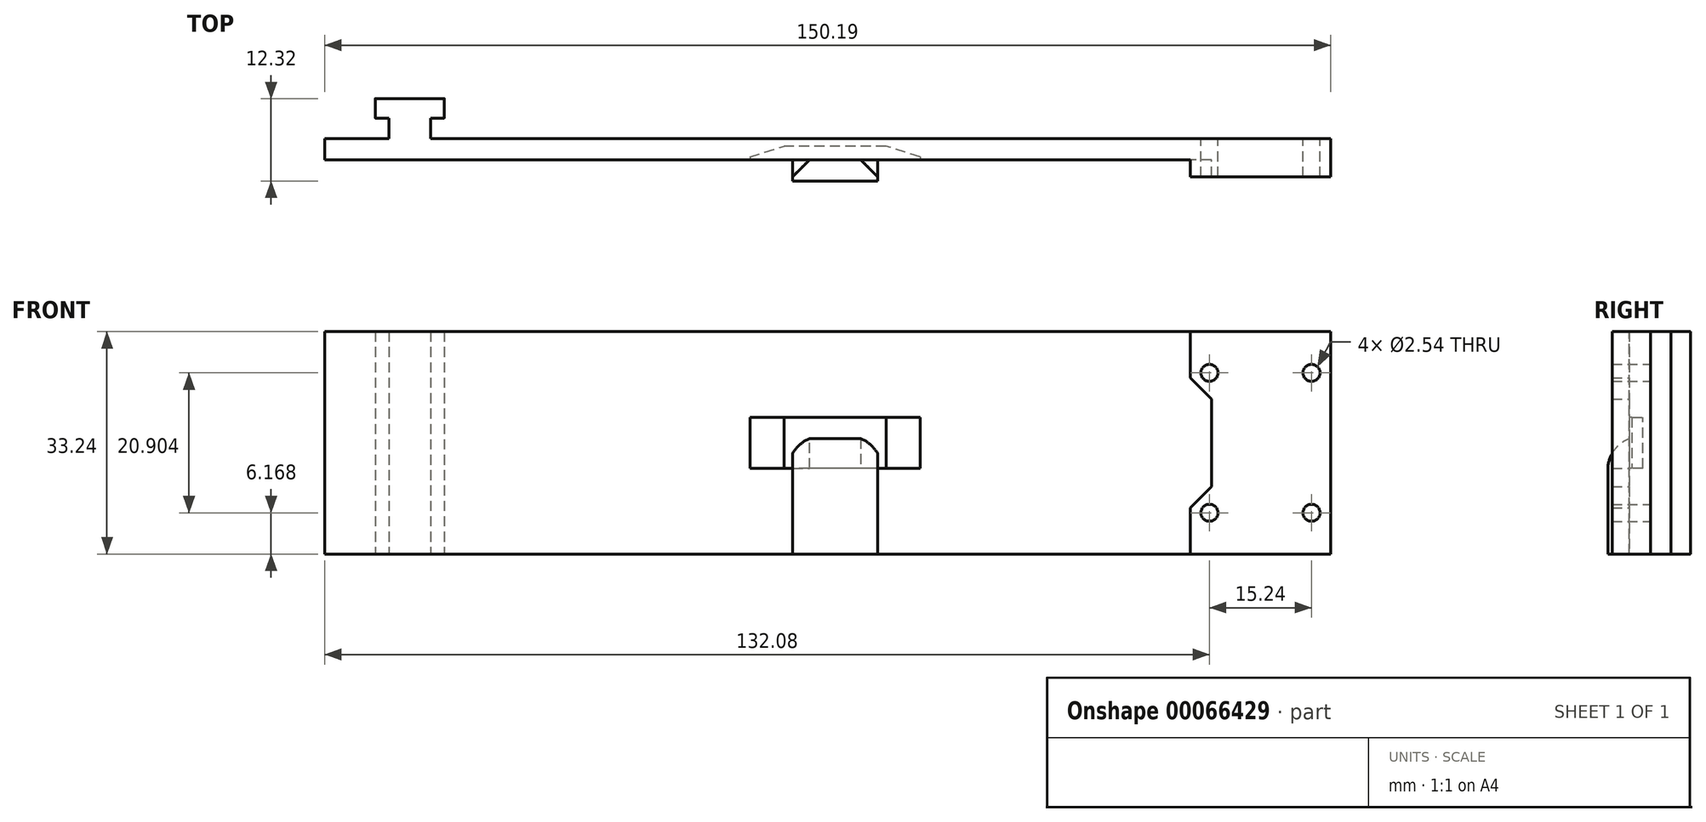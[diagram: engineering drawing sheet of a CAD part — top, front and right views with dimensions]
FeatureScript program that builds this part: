
annotation { "Feature Type Name" : "Feature", "Feature Type Description" : "" }
export const myFeature = defineFeature(function(context is Context, id is Id, definition is map)
    precondition{}
    {
        {
            var Q0;
            Q0=qCreatedBy(makeId("Front.planeOp"),FACE);
            var sketch = newSketch(context, id + "F0", { "sketchPlane" : qUnion([Q0])});
            skLineSegment(sketch, "E0.rect.bottom", {"start": v(5.16, 16.62) * mm, "end": v(-5.16, 16.62) * mm});
            skLineSegment(sketch, "E0.rect.top", {"start": v(5.16, -16.62) * mm, "end": v(-5.16, -16.62) * mm});
            skLineSegment(sketch, "E0.rect.left", {"start": v(5.16, 16.62) * mm, "end": v(5.16, -16.62) * mm});
            skLineSegment(sketch, "E0.rect.right", {"start": v(-5.16, 16.62) * mm, "end": v(-5.16, -16.62) * mm});
            skPoint(sketch, "E0.rect.middle", {"position": v(0, 0) * mm});
            skSolve(sketch);
        }
        {
            var Q0;
            Q0 = qSketchRegion(id + "F0", true);
            extrude(context, id + "F1", {"entities" : qUnion([Q0]), "depth" : 2.92 * mm, "offsetDistance" : 25.4 * mm});
        }
        {
            var Q0;
            Q0=makeQuery(id+"F1.opExtrude","CAP_FACE",FACE,{"disambiguationData":[OSD([sQuery(id+"F0.wireOp",EDGE,"E0.rect.bottom"),sQuery(id+"F0.wireOp",EDGE,"E0.rect.top"),sQuery(id+"F0.wireOp",EDGE,"E0.rect.left"),sQuery(id+"F0.wireOp",EDGE,"E0.rect.right")])],"isStart":false});
            var sketch = newSketch(context, id + "F2", { "sketchPlane" : qUnion([Q0])});
            skLineSegment(sketch, "E1.rect.bottom", {"start": v(3.1, 16.62) * mm, "end": v(-3.1, 16.62) * mm});
            skLineSegment(sketch, "E1.rect.top", {"start": v(3.1, -16.62) * mm, "end": v(-3.1, -16.62) * mm});
            skLineSegment(sketch, "E1.rect.left", {"start": v(3.1, 16.62) * mm, "end": v(3.1, -16.62) * mm});
            skLineSegment(sketch, "E1.rect.right", {"start": v(-3.1, 16.62) * mm, "end": v(-3.1, -16.62) * mm});
            skPoint(sketch, "E1.rect.middle", {"position": v(0, 0) * mm});
            skSolve(sketch);
        }
        {
            var Q0;
            Q0 = qSketchRegion(id + "F2", true);
            extrude(context, id + "F3", {"entities" : qUnion([Q0]), "operationType" : NewBodyOperationType.ADD, "depth" : 3.05 * mm, "offsetDistance" : 25.4 * mm});
        }
        {
            var Q0;
            Q0=makeQuery(id+"F3.opExtrude","CAP_FACE",FACE,{"disambiguationData":[OSD([sQuery(id+"F2.wireOp",EDGE,"E1.rect.bottom"),sQuery(id+"F2.wireOp",EDGE,"E1.rect.top"),sQuery(id+"F2.wireOp",EDGE,"E1.rect.left"),sQuery(id+"F2.wireOp",EDGE,"E1.rect.right")])],"isStart":false});
            var sketch = newSketch(context, id + "F4", { "sketchPlane" : qUnion([Q0])});
            skLineSegment(sketch, "E2.bottom", {"start": v(-12.7, -16.62) * mm, "end": v(137.5, -16.62) * mm});
            skLineSegment(sketch, "E2.top", {"start": v(-12.7, 16.62) * mm, "end": v(137.5, 16.62) * mm});
            skLineSegment(sketch, "E2.left", {"start": v(-12.7, -16.62) * mm, "end": v(-12.7, 16.62) * mm});
            skLineSegment(sketch, "E2.right", {"start": v(137.5, -16.62) * mm, "end": v(137.5, 16.62) * mm});
            skCircle(sketch, "E3", {"center": v(134.62, 10.45) * mm, "radius": 1.27 * mm});
            skCircle(sketch, "E4", {"center": v(134.62, -10.45) * mm, "radius": 1.27 * mm});
            skCircle(sketch, "E5", {"center": v(119.38, -10.45) * mm, "radius": 1.27 * mm});
            skCircle(sketch, "E6", {"center": v(119.38, 10.45) * mm, "radius": 1.27 * mm});
            skLineSegment(sketch, "E7", {"start": v(119.38, -10.45) * mm, "end": v(134.62, -10.45) * mm, "construction": true});
            skPoint(sketch, "E8", {"position": v(127, -10.45) * mm});
            skLineSegment(sketch, "E9", {"start": v(134.62, 10.45) * mm, "end": v(134.62, -10.45) * mm, "construction": true});
            skPoint(sketch, "E10", {"position": v(134.62, 0) * mm});
            skSolve(sketch);
        }
        {
            var Q0;
            Q0 = qSketchRegion(id + "F4", true);
            extrude(context, id + "F5", {"entities" : qUnion([Q0]), "operationType" : NewBodyOperationType.ADD, "depth" : 3.17 * mm});
        }
        {
            var Q0;
            Q0=makeQuery(id+"F1.opExtrude","CAP_EDGE",EDGE,{"disambiguationData":[OSD([sQuery(id+"F0.wireOp",EDGE,"E0.rect.left")])],"isStart":false});
            var Q1;
            Q1=makeQuery(id+"F1.opExtrude","CAP_EDGE",EDGE,{"disambiguationData":[OSD([sQuery(id+"F0.wireOp",EDGE,"E0.rect.left")])],"isStart":true});
            var Q2;
            Q2=makeQuery(id+"F1.opExtrude","CAP_EDGE",EDGE,{"disambiguationData":[OSD([sQuery(id+"F0.wireOp",EDGE,"E0.rect.right")])],"isStart":false});
            var Q3;
            Q3=makeQuery(id+"F1.opExtrude","CAP_EDGE",EDGE,{"disambiguationData":[OSD([sQuery(id+"F0.wireOp",EDGE,"E0.rect.right")])],"isStart":true});
            var Q4;
            Q4=makeQuery(id+"F1.opExtrude","CAP_EDGE",EDGE,{"disambiguationData":[OSD([sQuery(id+"F0.wireOp",EDGE,"E0.rect.top")])],"isStart":true});
            var Q5;
            Q5=makeQuery(id+"F1.opExtrude","CAP_EDGE",EDGE,{"disambiguationData":[OSD([sQuery(id+"F0.wireOp",EDGE,"E0.rect.bottom")])],"isStart":true});
            fillet(context, id + "F6", {"entities" : qUnion([Q0, Q1, Q2, Q3, Q4, Q5]), "radius" : .63 / 50.8 * mm, "tangentPropagation" : true, "allowEdgeOverflow" : false});
        }
        {
            var Q0;
            Q0=makeQuery(id+"F5.opExtrude","CAP_FACE",FACE,{"disambiguationData":[OSD([sQuery(id+"F4.wireOp",EDGE,"E2.bottom"),sQuery(id+"F4.wireOp",EDGE,"E2.top"),sQuery(id+"F4.wireOp",EDGE,"E2.left"),sQuery(id+"F4.wireOp",EDGE,"E2.right"),sQuery(id+"F4.wireOp",EDGE,"E3"),sQuery(id+"F4.wireOp",EDGE,"E4"),sQuery(id+"F4.wireOp",EDGE,"E5"),sQuery(id+"F4.wireOp",EDGE,"E6")])],"isStart":false});
            var sketch = newSketch(context, id + "F7", { "sketchPlane" : qUnion([Q0])});
            skLineSegment(sketch, "E11.rect.bottom", {"start": v(76.2, 3.81) * mm, "end": v(50.8, 3.81) * mm});
            skLineSegment(sketch, "E11.rect.top", {"start": v(76.2, -3.8) * mm, "end": v(50.8, -3.8) * mm});
            skLineSegment(sketch, "E11.rect.left", {"start": v(76.2, 3.81) * mm, "end": v(76.2, -3.8) * mm});
            skLineSegment(sketch, "E11.rect.right", {"start": v(50.8, 3.81) * mm, "end": v(50.8, -3.8) * mm});
            skPoint(sketch, "E11.rect.middle", {"position": v(63.5, 0) * mm});
            skLineSegment(sketch, "E12", {"start": v(0, 0) * mm, "end": v(63.5, 0) * mm, "construction": true});
            skSolve(sketch);
        }
        {
            var Q0;
            Q0 = qSketchRegion(id + "F7", true);
            extrude(context, id + "F8", {"entities" : qUnion([Q0]), "operationType" : NewBodyOperationType.REMOVE, "oppositeDirection" : true, "depth" : 2.03 * mm});
        }
        {
            var Q0;
            Q0=makeQuery(id+"F8.boolean.opBoolean","COPY",EDGE,{"derivedFrom":makeQuery(id+"F8.opExtrude","CAP_EDGE",EDGE,{"disambiguationData":[OSD([sQuery(id+"F7.wireOp",EDGE,"E11.rect.right")])],"isStart":false})});
            var Q1;
            Q1=makeQuery(id+"F8.boolean.opBoolean","COPY",EDGE,{"derivedFrom":makeQuery(id+"F8.opExtrude","CAP_EDGE",EDGE,{"disambiguationData":[OSD([sQuery(id+"F7.wireOp",EDGE,"E11.rect.left")])],"isStart":false})});
            chamfer(context, id + "F9", {"entities" : qUnion([Q0, Q1]), "chamferType" : ChamferType.TWO_OFFSETS, "width1" : 5.08 * mm, "oppositeDirection" : false, "width2" : 1.6 * mm, "tangentPropagation" : true});
        }
        {
            var Q0;
            Q0=makeQuery(id+"F5.opExtrude","CAP_FACE",FACE,{"disambiguationData":[OSD([sQuery(id+"F4.wireOp",EDGE,"E2.bottom"),sQuery(id+"F4.wireOp",EDGE,"E2.top"),sQuery(id+"F4.wireOp",EDGE,"E2.left"),sQuery(id+"F4.wireOp",EDGE,"E2.right"),sQuery(id+"F4.wireOp",EDGE,"E3"),sQuery(id+"F4.wireOp",EDGE,"E4"),sQuery(id+"F4.wireOp",EDGE,"E5"),sQuery(id+"F4.wireOp",EDGE,"E6")])],"isStart":false});
            var sketch = newSketch(context, id + "F10", { "sketchPlane" : qUnion([Q0])});
            skLineSegment(sketch, "E13.bottom", {"start": v(57.15, -16.62) * mm, "end": v(69.85, -16.62) * mm});
            skLineSegment(sketch, "E13.top", {"start": v(57.15, 0.64) * mm, "end": v(69.85, 0.64) * mm});
            skLineSegment(sketch, "E13.left", {"start": v(57.15, -16.62) * mm, "end": v(57.15, 0.64) * mm});
            skLineSegment(sketch, "E13.right", {"start": v(69.85, -16.62) * mm, "end": v(69.85, 0.64) * mm});
            skPoint(sketch, "E14", {"position": v(63.5, -3.8) * mm});
            skPoint(sketch, "E15", {"position": v(63.5, 0.64) * mm});
            skSolve(sketch);
        }
        {
            var Q0;
            Q0 = qSketchRegion(id + "F10", true);
            extrude(context, id + "F11", {"entities" : qUnion([Q0]), "operationType" : NewBodyOperationType.ADD, "depth" : 3.17 * mm});
        }
        {
            var Q0;
            Q0=makeQuery(id+"F11.opExtrude","CAP_EDGE",EDGE,{"disambiguationData":[OSD([sQuery(id+"F10.wireOp",EDGE,"E13.top")])],"isStart":false});
            fillet(context, id + "F12", {"entities" : qUnion([Q0]), "radius" : 5.08 * mm, "tangentPropagation" : true, "allowEdgeOverflow" : false});
        }
        {
            var Q0;
            Q0=makeQuery(id+"F5.opExtrude","CAP_FACE",FACE,{"disambiguationData":[OSD([sQuery(id+"F4.wireOp",EDGE,"E2.bottom"),sQuery(id+"F4.wireOp",EDGE,"E2.top"),sQuery(id+"F4.wireOp",EDGE,"E2.left"),sQuery(id+"F4.wireOp",EDGE,"E2.right"),sQuery(id+"F4.wireOp",EDGE,"E3"),sQuery(id+"F4.wireOp",EDGE,"E4"),sQuery(id+"F4.wireOp",EDGE,"E5"),sQuery(id+"F4.wireOp",EDGE,"E6")])],"isStart":false});
            var sketch = newSketch(context, id + "F13", { "sketchPlane" : qUnion([Q0])});
            skCircle(sketch, "E16", {"center": v(119.38, 10.45) * mm, "radius": 1.27 * mm});
            skCircle(sketch, "E17", {"center": v(134.62, 10.45) * mm, "radius": 1.27 * mm});
            skCircle(sketch, "E18", {"center": v(119.38, -10.45) * mm, "radius": 1.27 * mm});
            skCircle(sketch, "E19", {"center": v(134.62, -10.45) * mm, "radius": 1.27 * mm});
            skLineSegment(sketch, "E20.bottom", {"start": v(137.5, 16.62) * mm, "end": v(116.5, 16.62) * mm});
            skLineSegment(sketch, "E20.top", {"start": v(137.5, -16.62) * mm, "end": v(116.5, -16.62) * mm});
            skLineSegment(sketch, "E20.left", {"start": v(137.5, 16.62) * mm, "end": v(137.5, -16.62) * mm});
            skLineSegment(sketch, "E21", {"start": v(116.5, 16.62) * mm, "end": v(116.5, 9.73) * mm});
            skLineSegment(sketch, "E22", {"start": v(116.5, 9.73) * mm, "end": v(119.68, 6.56) * mm});
            skLineSegment(sketch, "E23", {"start": v(119.68, 6.56) * mm, "end": v(119.68, -6.56) * mm});
            skLineSegment(sketch, "E24", {"start": v(119.68, -6.56) * mm, "end": v(116.5, -9.73) * mm});
            skLineSegment(sketch, "E25", {"start": v(116.5, -9.73) * mm, "end": v(116.5, -16.62) * mm});
            skSolve(sketch);
        }
        {
            var Q0;
            Q0 = qSketchRegion(id + "F13", true);
            extrude(context, id + "F14", {"entities" : qUnion([Q0]), "operationType" : NewBodyOperationType.ADD, "depth" : 2.54 * mm});
        }
        {
            var Q0;
            {var subQ0=sQuery(id+"F10.wireOp",EDGE,"E13.right");Q0=makeQuery(id+"F11.boolean.opBoolean","SPLIT",EDGE,{"disambiguationData":[topologyDisambiguationEdgeConnected([makeQuery(id+"F5.opExtrude","CAP_FACE",FACE,{"disambiguationData":[OSD([sQuery(id+"F4.wireOp",EDGE,"E2.bottom"),sQuery(id+"F4.wireOp",EDGE,"E2.top"),sQuery(id+"F4.wireOp",EDGE,"E2.left"),sQuery(id+"F4.wireOp",EDGE,"E2.right"),sQuery(id+"F4.wireOp",EDGE,"E3"),sQuery(id+"F4.wireOp",EDGE,"E4"),sQuery(id+"F4.wireOp",EDGE,"E5"),sQuery(id+"F4.wireOp",EDGE,"E6")])],"isStart":false})])],"derivedFrom":makeQuery(id+"F11.opExtrude","CAP_EDGE",EDGE,{"disambiguationData":[OSD([subQ0])],"isStart":true})});}
            var Q1;
            {var subQ0=sQuery(id+"F10.wireOp",EDGE,"E13.left");Q1=makeQuery(id+"F11.boolean.opBoolean","SPLIT",EDGE,{"disambiguationData":[topologyDisambiguationEdgeConnected([makeQuery(id+"F5.opExtrude","CAP_FACE",FACE,{"disambiguationData":[OSD([sQuery(id+"F4.wireOp",EDGE,"E2.bottom"),sQuery(id+"F4.wireOp",EDGE,"E2.top"),sQuery(id+"F4.wireOp",EDGE,"E2.left"),sQuery(id+"F4.wireOp",EDGE,"E2.right"),sQuery(id+"F4.wireOp",EDGE,"E3"),sQuery(id+"F4.wireOp",EDGE,"E4"),sQuery(id+"F4.wireOp",EDGE,"E5"),sQuery(id+"F4.wireOp",EDGE,"E6")])],"isStart":false})])],"derivedFrom":makeQuery(id+"F11.opExtrude","CAP_EDGE",EDGE,{"disambiguationData":[OSD([subQ0])],"isStart":true})});}
            chamfer(context, id + "F15", {"entities" : qUnion([Q0, Q1]), "width" : 2.54 * mm, "tangentPropagation" : true});
        }
    });
